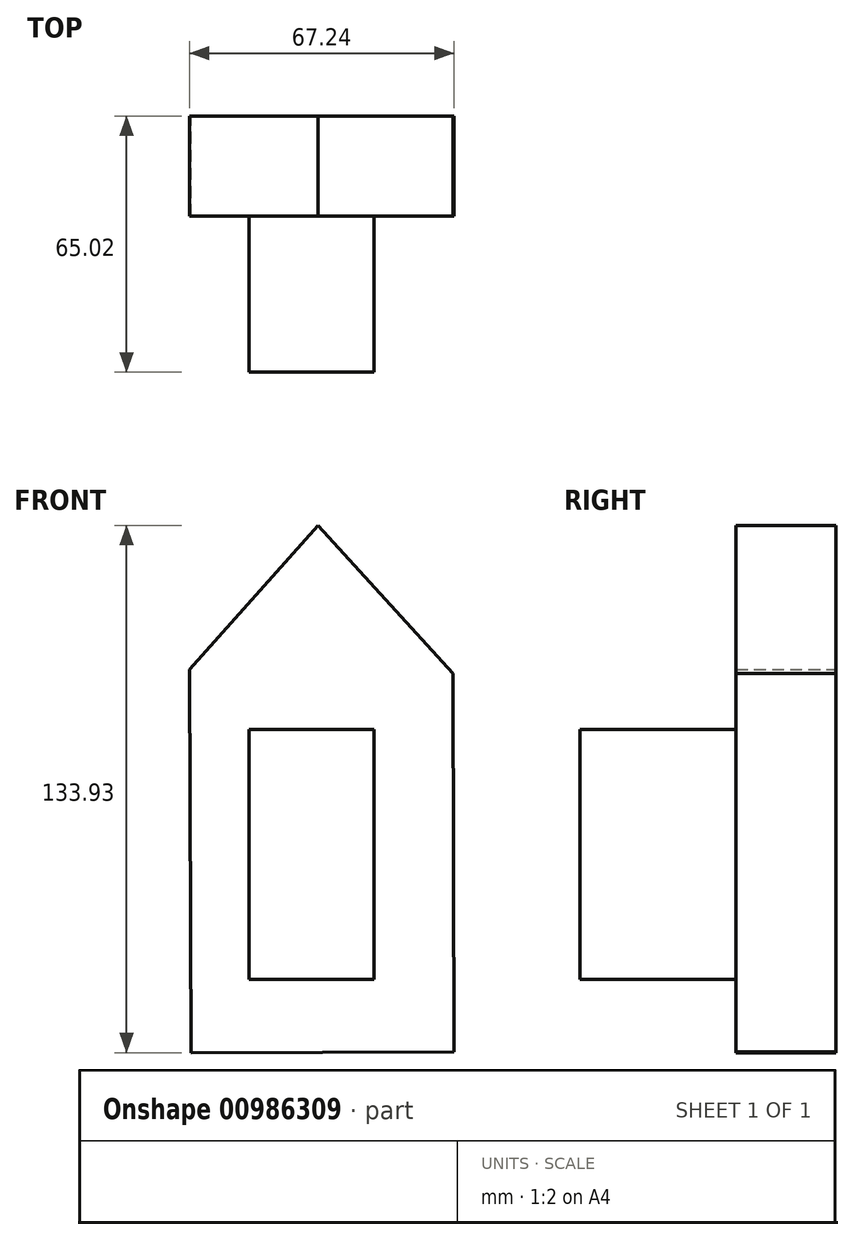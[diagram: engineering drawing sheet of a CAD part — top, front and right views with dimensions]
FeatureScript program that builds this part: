
annotation { "Feature Type Name" : "Feature", "Feature Type Description" : "" }
export const myFeature = defineFeature(function(context is Context, id is Id, definition is map)
    precondition{}
    {
        {
            var Q0;
            Q0=qCreatedBy(makeId("Front.planeOp"),FACE);
            var sketch = newSketch(context, id + "F0", { "sketchPlane" : qUnion([Q0])});
            skLineSegment(sketch, "E0", {"start": v(-32.22, -56.02) * mm, "end": v(34.56, -55.8) * mm});
            skLineSegment(sketch, "E1", {"start": v(34.56, -55.8) * mm, "end": v(34.25, 40.39) * mm});
            skLineSegment(sketch, "E2", {"start": v(34.25, 40.39) * mm, "end": v(0, 77.9) * mm});
            skLineSegment(sketch, "E3", {"start": v(0, 77.9) * mm, "end": v(-32.68, 41.37) * mm});
            skLineSegment(sketch, "E4", {"start": v(-32.68, 41.37) * mm, "end": v(-32.22, -56.02) * mm});
            skSolve(sketch);
        }
        {
            var Q0;
            Q0 = qSketchRegion(id + "F0", true);
            extrude(context, id + "F1", {"entities" : qUnion([Q0]), "depth" : 25.4 * mm, "offsetDistance" : 25.4 * mm});
        }
        {
            var Q0;
            Q0=makeQuery(id+"F1.opExtrude","CAP_FACE",FACE,{"disambiguationData":[OSD([sQuery(id+"F0.wireOp",EDGE,"E0"),sQuery(id+"F0.wireOp",EDGE,"E1"),sQuery(id+"F0.wireOp",EDGE,"E2"),sQuery(id+"F0.wireOp",EDGE,"E3"),sQuery(id+"F0.wireOp",EDGE,"E4")])],"isStart":false});
            var sketch = newSketch(context, id + "F2", { "sketchPlane" : qUnion([Q0])});
            skLineSegment(sketch, "E5.bottom", {"start": v(-17.48, 26.15) * mm, "end": v(14.27, 26.15) * mm});
            skLineSegment(sketch, "E5.top", {"start": v(-17.48, -37.35) * mm, "end": v(14.27, -37.35) * mm});
            skLineSegment(sketch, "E5.left", {"start": v(-17.48, 26.15) * mm, "end": v(-17.48, -37.35) * mm});
            skLineSegment(sketch, "E5.right", {"start": v(14.27, 26.15) * mm, "end": v(14.27, -37.35) * mm});
            skSolve(sketch);
        }
        {
            var Q0;
            Q0 = qSketchRegion(id + "F2", true);
            extrude(context, id + "F3", {"entities" : qUnion([Q0]), "operationType" : NewBodyOperationType.ADD, "depth" : 39.62 * mm, "offsetDistance" : 25.4 * mm});
        }
    });
